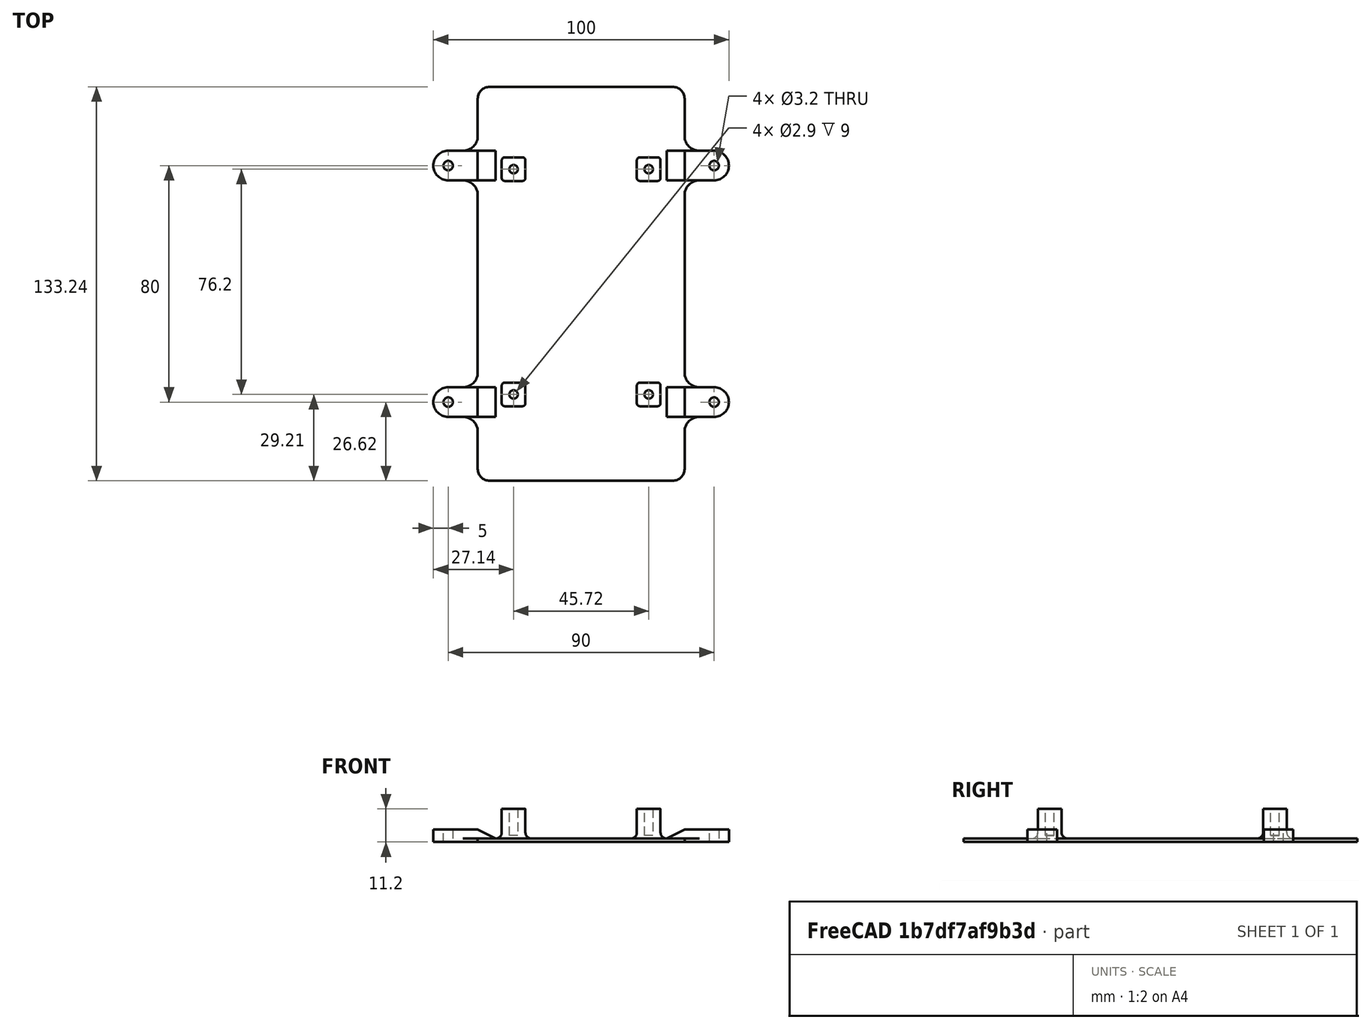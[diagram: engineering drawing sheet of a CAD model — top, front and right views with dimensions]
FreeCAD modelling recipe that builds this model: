
FCSTD DOCUMENT  (FreeCAD 0.18.4R)
Label: Nucleo-F746ZG-Holder
License: All rights reserved
LicenseURL: http://en.wikipedia.org/wiki/All_rights_reserved
objects: Sketcher::SketchObject×8, PartDesign::Pad×5, PartDesign::Mirrored×4, PartDesign::Fillet×4, PartDesign::Pocket×2, PartDesign::Body×1, Mesh::Feature×1
note: 31 computed .brp shape members not serialized (recipe doc carries the construction recipe); baked Part::Feature solids carry a one-line shape summary decoded from their .brp

FEATURE [Sketcher::SketchObject] Sketch
  MapMode = 5
  Support = -> [XY_Plane]
  sketch-geometry (12):
    g0: LineSegment StartX=-35 StartY=66.62 StartZ=0 EndX=35 EndY=66.62 EndZ=0
    g1: LineSegment StartX=35 StartY=66.62 StartZ=0 EndX=35 EndY=-66.62 EndZ=0
    g2: LineSegment StartX=35 StartY=-66.62 StartZ=0 EndX=-35 EndY=-66.62 EndZ=0
    g3: LineSegment StartX=-35 StartY=-66.62 StartZ=0 EndX=-35 EndY=66.62 EndZ=0
    g4: LineSegment StartX=-22.86 StartY=38.79 StartZ=0 EndX=22.86 EndY=38.79 EndZ=0
    g5: LineSegment StartX=22.86 StartY=38.79 StartZ=0 EndX=22.86 EndY=-37.41 EndZ=0
    g6: LineSegment StartX=22.86 StartY=-37.41 StartZ=0 EndX=-22.86 EndY=-37.41 EndZ=0
    g7: LineSegment StartX=-22.86 StartY=-37.41 StartZ=0 EndX=-22.86 EndY=38.79 EndZ=0
    g8: LineSegment StartX=-45 StartY=45 StartZ=0 EndX=45 EndY=45 EndZ=0
    g9: LineSegment StartX=45 StartY=45 StartZ=0 EndX=45 EndY=-45 EndZ=0
    g10: LineSegment StartX=45 StartY=-45 StartZ=0 EndX=-45 EndY=-45 EndZ=0
    g11: LineSegment StartX=-45 StartY=-45 StartZ=0 EndX=-45 EndY=45 EndZ=0
  constraints (34):
    c: Coincident(g0,g1)
    c: Coincident(g1,g2)
    c: Coincident(g2,g3)
    c: Coincident(g3,g0)
    c: Horizontal(g0)
    c: Horizontal(g2)
    c: Vertical(g1)
    c: Vertical(g3)
    c: DistanceX(g2,g2) = 70
    c: DistanceY(g1,g1) = 133.24
    c: Symmetric(g1,g0,g-1)
    c: Coincident(g4,g5)
    c: Coincident(g5,g6)
    c: Coincident(g6,g7)
    c: Coincident(g7,g4)
    c: Horizontal(g4)
    c: Horizontal(g6)
    c: Vertical(g5)
    c: Vertical(g7)
    c: DistanceY(g2,g6) = 29.21
    c: DistanceX(g6,g6) = 45.72
    c: DistanceX(g-1,g5) = 22.86
    c: DistanceY(g2,g4) = 105.41
    c: Coincident(g8,g9)
    c: Coincident(g9,g10)
    c: Coincident(g10,g11)
    c: Coincident(g11,g8)
    c: Horizontal(g8)
    c: Horizontal(g10)
    c: Vertical(g9)
    c: Vertical(g11)
    c: Symmetric(g9,g8,g-1)
    c: Equal(g10,g9)
    c: DistanceX(g8,g8) = 90
FEATURE [Sketcher::SketchObject] Sketch001
  ExternalGeometry = -> [Sketch]
  MapMode = 5
  Support = -> [XY_Plane]
  sketch-geometry (20):
    g0: LineSegment StartX=-35 StartY=66.62 StartZ=0 EndX=35 EndY=66.62 EndZ=0
    g1: LineSegment StartX=35 StartY=45 StartZ=0 EndX=45 EndY=45 EndZ=0
    g2: LineSegment StartX=35 StartY=45 StartZ=0 EndX=35 EndY=66.62 EndZ=0
    g3: LineSegment StartX=45 StartY=35 StartZ=0 EndX=35 EndY=35 EndZ=0
    g4: LineSegment StartX=35 StartY=35 StartZ=0 EndX=35 EndY=-35 EndZ=0
    g5: LineSegment StartX=35 StartY=-35 StartZ=0 EndX=45 EndY=-35 EndZ=0
    g6: LineSegment StartX=45 StartY=-45 StartZ=0 EndX=35 EndY=-45 EndZ=0
    g7: LineSegment StartX=35 StartY=-45 StartZ=0 EndX=35 EndY=-66.62 EndZ=0
    g8: LineSegment StartX=35 StartY=-66.62 StartZ=0 EndX=-35 EndY=-66.62 EndZ=0
    g9: LineSegment StartX=-35 StartY=-66.62 StartZ=0 EndX=-35 EndY=-45 EndZ=0
    g10: LineSegment StartX=-35 StartY=-45 StartZ=0 EndX=-45 EndY=-45 EndZ=0
    g11: LineSegment StartX=-45 StartY=-35 StartZ=0 EndX=-35 EndY=-35 EndZ=0
    g12: LineSegment StartX=-35 StartY=-35 StartZ=0 EndX=-35 EndY=35 EndZ=0
    g13: LineSegment StartX=-35 StartY=35 StartZ=0 EndX=-45 EndY=35 EndZ=0
    g14: LineSegment StartX=-45 StartY=45 StartZ=0 EndX=-35 EndY=45 EndZ=0
    g15: LineSegment StartX=-35 StartY=45 StartZ=0 EndX=-35 EndY=66.62 EndZ=0
    g16: ArcOfCircle CenterX=45 CenterY=40 CenterZ=0 NormalX=0 NormalY=0 NormalZ=1 AngleXU=0 Radius=5 StartAngle=4.71239 EndAngle=7.85398
    g17: ArcOfCircle CenterX=-45 CenterY=40 CenterZ=0 NormalX=0 NormalY=0 NormalZ=1 AngleXU=0 Radius=5 StartAngle=1.5708 EndAngle=4.71239
    g18: ArcOfCircle CenterX=-45 CenterY=-40 CenterZ=0 NormalX=0 NormalY=0 NormalZ=1 AngleXU=0 Radius=5 StartAngle=1.5708 EndAngle=4.71239
    g19: ArcOfCircle CenterX=45 CenterY=-40 CenterZ=0 NormalX=0 NormalY=0 NormalZ=1 AngleXU=0 Radius=5 StartAngle=4.71239 EndAngle=7.85398
  constraints (52):
    c: Coincident(g2,g-6)
    c: Coincident(g0,g2)
    c: Coincident(g0,g-6)
    c: Coincident(g3,g4)
    c: Coincident(g4,g5)
    c: Coincident(g6,g7)
    c: Coincident(g7,g8)
    c: Coincident(g8,g9)
    c: Coincident(g9,g10)
    c: Coincident(g11,g12)
    c: Coincident(g12,g13)
    c: Coincident(g14,g15)
    c: Coincident(g15,g0)
    c: PointOnObject(g14,g-3)
    c: Vertical(g15)
    c: Coincident(g14,g-3)
    c: Vertical(g13,g14)
    c: Horizontal(g13)
    c: Vertical(g12,g14)
    c: Vertical(g12)
    c: Horizontal(g11)
    c: Coincident(g-4,g10)
    c: Horizontal(g10)
    c: Horizontal(g6)
    c: Coincident(g6,g-4)
    c: Vertical(g7)
    c: Coincident(g7,g-5)
    c: Coincident(g8,g-5)
    c: Vertical(g9,g11)
    c: Vertical(g5,g6)
    c: Horizontal(g5)
    c: Vertical(g4)
    c: Vertical(g4,g6)
    c: Horizontal(g3)
    c: Vertical(g3,g1)
    c: Coincident(g1,g-3)
    c: PointOnObject(g1,g-3)
    c: Vertical(g2)
    c: Coincident(g2,g1)
    c: Tangent(g16,g1) = 1.5708
    c: Coincident(g16,g3)
    c: Radius(g16) = 5
    c: Tangent(g17,g14) = 1.5708
    c: Coincident(g17,g13)
    c: Radius(g17) = 5
    c: Tangent(g11,g18) = 1.5708
    c: Coincident(g18,g10)
    c: Vertical(g11,g10)
    c: Radius(g18) = 5
    c: Coincident(g19,g5)
    c: Tangent(g19,g6) = 1.5708
    c: Radius(g19) = 5
FEATURE [PartDesign::Pad] Pad
  Length = 1.2
  Length2 = 100
  Profile = -> Sketch001
  Type = 0
FEATURE [Sketcher::SketchObject] Sketch002
  ExternalGeometry = -> [Pad]
  MapMode = 5
  Placement = pos=(0,0,1.2) rot=(0,0,1;0rad)
  Support = -> [Pad]
  sketch-geometry (8):
    g0: LineSegment StartX=35 StartY=45 StartZ=0 EndX=35 EndY=35 EndZ=0
    g1: LineSegment StartX=35 StartY=45 StartZ=0 EndX=45 EndY=45 EndZ=0
    g2: LineSegment StartX=35 StartY=35 StartZ=0 EndX=45 EndY=35 EndZ=0
    g3: ArcOfCircle CenterX=45 CenterY=40 CenterZ=0 NormalX=0 NormalY=0 NormalZ=1 AngleXU=0 Radius=5 StartAngle=4.71238 EndAngle=7.85399
    g4: ArcOfCircle CenterX=-45 CenterY=40 CenterZ=0 NormalX=0 NormalY=0 NormalZ=1 AngleXU=0 Radius=5 StartAngle=1.5708 EndAngle=4.71239
    g5: LineSegment StartX=-45 StartY=45 StartZ=0 EndX=-35 EndY=45 EndZ=0
    g6: LineSegment StartX=-35 StartY=45 StartZ=0 EndX=-35 EndY=35 EndZ=0
    g7: LineSegment StartX=-35 StartY=35 StartZ=0 EndX=-45 EndY=35 EndZ=0
  constraints (18):
    c: Coincident(g0,g-4)
    c: Coincident(g0,g-5)
    c: Coincident(g7,g-7)
    c: Coincident(g7,g-6)
    c: Coincident(g6,g7)
    c: Coincident(g6,g-8)
    c: Coincident(g5,g6)
    c: Coincident(g-8,g5)
    c: Coincident(g4,g5)
    c: Coincident(g4,g7)
    c: Equal(g4,g-7)
    c: Coincident(g3,g-5)
    c: Coincident(g2,g3)
    c: Coincident(g2,g0)
    c: Coincident(g1,g0)
    c: Coincident(g-4,g1)
    c: Coincident(g3,g1)
    c: Equal(g-3,g3)
FEATURE [PartDesign::Pad] Pad001
  BaseFeature = -> Pad
  Length = 3
  Length2 = 100
  Profile = -> Sketch002
  Type = 0
FEATURE [PartDesign::Mirrored] Mirrored
  BaseFeature = -> Pad001
  MirrorPlane = -> XZ_Plane
  Originals = -> [Pad001]
FEATURE [Sketcher::SketchObject] Sketch003
  ExternalGeometry = -> [Sketch,Mirrored]
  MapMode = 5
  Placement = pos=(0,0,4.2) rot=(0,0,1;0rad)
  Support = -> [Mirrored]
  sketch-geometry (2):
    g0: Circle CenterX=-45 CenterY=40 CenterZ=0 NormalX=0 NormalY=0 NormalZ=1 AngleXU=0 Radius=1.6
    g1: Circle CenterX=45 CenterY=40 CenterZ=0 NormalX=0 NormalY=0 NormalZ=1 AngleXU=0 Radius=1.6
  constraints (4):
    c: Equal(g1,g0)
    c: Radius(g0) = 1.6
    c: Coincident(g0,g-4)
    c: Coincident(g1,g-5)
FEATURE [PartDesign::Pocket] Pocket
  BaseFeature = -> Mirrored
  Length = 5
  Length2 = 100
  Profile = -> Sketch003
  Type = 1
FEATURE [PartDesign::Mirrored] Mirrored001
  BaseFeature = -> Pocket
  MirrorPlane = -> XZ_Plane
  Originals = -> [Pocket]
FEATURE [Sketcher::SketchObject] Sketch004
  ExternalGeometry = -> [Sketch]
  MapMode = 5
  Placement = pos=(0,0,1.2) rot=(0,0,1;0rad)
  Support = -> [Mirrored001]
  sketch-geometry (16):
    g0: LineSegment StartX=-26.86 StartY=42.79 StartZ=0 EndX=-18.86 EndY=42.79 EndZ=0
    g1: LineSegment StartX=-18.86 StartY=42.79 StartZ=0 EndX=-18.86 EndY=34.79 EndZ=0
    g2: LineSegment StartX=-18.86 StartY=34.79 StartZ=0 EndX=-26.86 EndY=34.79 EndZ=0
    g3: LineSegment StartX=-26.86 StartY=34.79 StartZ=0 EndX=-26.86 EndY=42.79 EndZ=0
    g4: LineSegment StartX=18.86 StartY=42.79 StartZ=0 EndX=26.86 EndY=42.79 EndZ=0
    g5: LineSegment StartX=26.86 StartY=42.79 StartZ=0 EndX=26.86 EndY=34.79 EndZ=0
    g6: LineSegment StartX=26.86 StartY=34.79 StartZ=0 EndX=18.86 EndY=34.79 EndZ=0
    g7: LineSegment StartX=18.86 StartY=34.79 StartZ=0 EndX=18.86 EndY=42.79 EndZ=0
    g8: LineSegment StartX=18.86 StartY=-33.41 StartZ=0 EndX=26.86 EndY=-33.41 EndZ=0
    g9: LineSegment StartX=26.86 StartY=-33.41 StartZ=0 EndX=26.86 EndY=-41.41 EndZ=0
    g10: LineSegment StartX=26.86 StartY=-41.41 StartZ=0 EndX=18.86 EndY=-41.41 EndZ=0
    g11: LineSegment StartX=18.86 StartY=-41.41 StartZ=0 EndX=18.86 EndY=-33.41 EndZ=0
    g12: LineSegment StartX=-26.86 StartY=-33.41 StartZ=0 EndX=-18.86 EndY=-33.41 EndZ=0
    g13: LineSegment StartX=-18.86 StartY=-33.41 StartZ=0 EndX=-18.86 EndY=-41.41 EndZ=0
    g14: LineSegment StartX=-18.86 StartY=-41.41 StartZ=0 EndX=-26.86 EndY=-41.41 EndZ=0
    g15: LineSegment StartX=-26.86 StartY=-41.41 StartZ=0 EndX=-26.86 EndY=-33.41 EndZ=0
  constraints (44):
    c: Coincident(g0,g1)
    c: Coincident(g1,g2)
    c: Coincident(g2,g3)
    c: Coincident(g3,g0)
    c: Horizontal(g0)
    c: Horizontal(g2)
    c: Vertical(g1)
    c: Vertical(g3)
    c: Coincident(g4,g5)
    c: Coincident(g5,g6)
    c: Coincident(g6,g7)
    c: Coincident(g7,g4)
    c: Horizontal(g4)
    c: Horizontal(g6)
    c: Vertical(g5)
    c: Vertical(g7)
    c: Equal(g6,g5)
    c: Equal(g5,g2)
    c: Equal(g2,g1)
    c: Symmetric(g5,g4,g-3)
    c: Symmetric(g1,g0,g-3)
    c: DistanceX(g2,g2) = 8
    c: Coincident(g8,g9)
    c: Coincident(g9,g10)
    c: Coincident(g10,g11)
    c: Coincident(g11,g8)
    c: Horizontal(g8)
    c: Horizontal(g10)
    c: Vertical(g9)
    c: Vertical(g11)
    c: Coincident(g12,g13)
    c: Coincident(g13,g14)
    c: Coincident(g14,g15)
    c: Coincident(g15,g12)
    c: Horizontal(g12)
    c: Horizontal(g14)
    c: Vertical(g13)
    c: Vertical(g15)
    c: Equal(g14,g13)
    c: Equal(g13,g10)
    c: Equal(g10,g11)
    c: Equal(g11,g6)
    c: Symmetric(g13,g12,g-4)
    c: Symmetric(g9,g8,g-4)
FEATURE [PartDesign::Pad] Pad002
  BaseFeature = -> Mirrored001
  Length = 10
  Length2 = 100
  Profile = -> Sketch004
  Type = 0
FEATURE [Sketcher::SketchObject] Sketch005
  ExternalGeometry = -> [Sketch]
  MapMode = 5
  Placement = pos=(0,0,11.2) rot=(0,0,1;0rad)
  Support = -> [Pad002]
  sketch-geometry (4):
    g0: Circle CenterX=-22.86 CenterY=38.79 CenterZ=0 NormalX=0 NormalY=0 NormalZ=1 AngleXU=0 Radius=1.45
    g1: Circle CenterX=22.86 CenterY=38.79 CenterZ=0 NormalX=0 NormalY=0 NormalZ=1 AngleXU=0 Radius=1.45
    g2: Circle CenterX=22.86 CenterY=-37.41 CenterZ=0 NormalX=0 NormalY=0 NormalZ=1 AngleXU=0 Radius=1.45
    g3: Circle CenterX=-22.86 CenterY=-37.41 CenterZ=0 NormalX=0 NormalY=0 NormalZ=1 AngleXU=0 Radius=1.45
  constraints (8):
    c: Equal(g3,g2)
    c: Equal(g2,g1)
    c: Equal(g1,g0)
    c: Coincident(g1,g-3)
    c: Coincident(g0,g-3)
    c: Coincident(g3,g-4)
    c: Coincident(g2,g-4)
    c: Diameter(g2) = 2.9
FEATURE [PartDesign::Pocket] Pocket001
  BaseFeature = -> Pad002
  Length = 9
  Length2 = 100
  Profile = -> Sketch005
  Type = 0
FEATURE [Sketcher::SketchObject] Sketch006
  ExternalGeometry = -> [Pocket001]
  MapMode = 5
  Placement = pos=(0,35,0) rot=(1,0,0;1.5708rad)
  Support = -> [Pocket001]
  sketch-geometry (3):
    g0: LineSegment StartX=35 StartY=4.2 StartZ=0 EndX=35 EndY=1.2 EndZ=0
    g1: LineSegment StartX=35 StartY=1.2 StartZ=0 EndX=29 EndY=1.2 EndZ=0
    g2: LineSegment StartX=29 StartY=1.2 StartZ=0 EndX=35 EndY=4.2 EndZ=0
  constraints (7):
    c: Coincident(g0,g1)
    c: Coincident(g1,g2)
    c: Coincident(g0,g-4)
    c: Coincident(g0,g-3)
    c: Coincident(g2,g0)
    c: PointOnObject(g1,g-4)
    c: DistanceX(g1,g1) = 6
FEATURE [PartDesign::Pad] Pad003
  BaseFeature = -> Pocket001
  Length = 10
  Length2 = 100
  Profile = -> Sketch006
  Reversed = true
  Type = 0
FEATURE [PartDesign::Mirrored] Mirrored002
  BaseFeature = -> Pad003
  MirrorPlane = -> Sketch006 [V_Axis]
  Originals = -> [Pad003]
FEATURE [Sketcher::SketchObject] Sketch007
  ExternalGeometry = -> [Mirrored002]
  MapMode = 5
  Placement = pos=(0,-45,0) rot=(1,0,0;1.5708rad)
  Support = -> [Mirrored002]
  sketch-geometry (3):
    g0: LineSegment StartX=29 StartY=1.2 StartZ=0 EndX=35 EndY=4.2 EndZ=0
    g1: LineSegment StartX=35 StartY=4.2 StartZ=0 EndX=35 EndY=1.2 EndZ=0
    g2: LineSegment StartX=35 StartY=1.2 StartZ=0 EndX=29 EndY=1.2 EndZ=0
  constraints (6):
    c: Coincident(g0,g1)
    c: Coincident(g1,g2)
    c: Coincident(g2,g-3)
    c: Coincident(g0,g2)
    c: Coincident(g0,g-4)
    c: Coincident(g1,g-4)
FEATURE [PartDesign::Pad] Pad004
  BaseFeature = -> Mirrored002
  Length = 10
  Length2 = 100
  Profile = -> Sketch007
  Reversed = true
  Type = 0
FEATURE [PartDesign::Mirrored] Mirrored003
  BaseFeature = -> Pad004
  MirrorPlane = -> Sketch007 [V_Axis]
  Originals = -> [Pad004]
FEATURE [PartDesign::Fillet] Fillet
  Base = -> Mirrored003 [Edge91,Edge89,Edge39,Edge8]
  BaseFeature = -> Mirrored003
  Radius = 4
FEATURE [PartDesign::Fillet] Fillet001
  Base = -> Fillet [Edge94,Edge102,Edge92,Edge81,Edge78,Edge3,Edge80,Edge90]
  BaseFeature = -> Fillet
  Radius = 5
FEATURE [PartDesign::Fillet] Fillet002
  Base = -> Fillet001 [Edge175,Edge173,Edge176,Edge179,Edge181,Edge183,Edge187,Edge184,Edge167,Edge165,Edge168,Edge192,Edge189,Edge191,Edge171,Edge195]
  BaseFeature = -> Fillet001
  Radius = 1
FEATURE [PartDesign::Fillet] Fillet003
  Base = -> Fillet002 [Edge49,Edge57,Edge65,Edge1]
  BaseFeature = -> Fillet002
  Radius = 2
FEATURE [PartDesign::Body] Body
  Group = -> [Sketch,Sketch001,Pad,Sketch002,Pad001,Mirrored,Sketch003,Pocket,Mirrored001,Sketch004,Pad002,Sketch005,Pocket001,Sketch006,Pad003,Mirrored002,Sketch007,Pad004,Mirrored003,Fillet,Fillet001,Fillet002,Fillet003]
  Origin = -> Origin
  Tip = -> Fillet003
FEATURE [Mesh::Feature] Mesh  label="Body (Meshed)"
